# Revit family: Микрофоны и микрофонные панели_АРИЯ
name_source: partatom
category: Системы пожарной сигнализации
revit_build: Autodesk Revit MEP 2016 (Build: 20151007_0715(x64)
units: mm (PartAtom-declared; Revit-internal decimal feet)

## family parameters
Всегда вертикально = Да
На основе рабочей плоскости = Нет
Общий = Нет
При загрузке вырезать с полостями = Нет
Размер круглого соединителя = Использовать диаметр
Сохранять ориентацию аннотаций = Нет
Тип детали = Нормальный
Точка расчета площади = Нет

## types (2) — shared parameters
ADSK_URL документации изделия = https://omelta.com
ADSK_URL страницы изделия = https://omelta.com
ADSK_Единица измерения = шт.
ADSK_Завод-изготовитель = г. Омск, ООО «Электротехника и Автоматика»
ADSK_Код изделия = 437245
ADSK_Напряжение = 12 В
ADSK_Размер_Высота = 218 мм
ADSK_Размер_Глубина = 90 мм
ADSK_Размер_Ширина = 136 мм
IP = 20
Диапазон рабочих температур = –20...+55 °С
Материал_Кнопки = ЭиА_Серый
Материал_Корпус = ЭиА_Микрофон
Материал_Надпись = ЭиА_Белый
Основание_Высота = 28 мм
Стойка_Смещение = 60 мм

## per-type parameters (varying)
| type | ADSK_Масса | ADSK_Наименование | ADSK_Номинальная мощность | ADSK_Обозначение | ADSK_Ток | Ария_МКП | Количество зон | МК-12 |
| АРИЯ-МКП-4 | 0.17 | Микрофонная панель | 1 Вт | Микрофонная панель четырехзональная | 50 мА | Да | 4 | Нет |
| МК-12 | 0 | Микрофон | 0 Вт | Микрофон трансляционный | 15 мА | Нет | 1 | Да |

note: column(s) folded — value = type name in every type: ADSK_Марка

## geometry (parser evidence)
native form markers: Blend x2
no freeform markers — native parametric forms only
